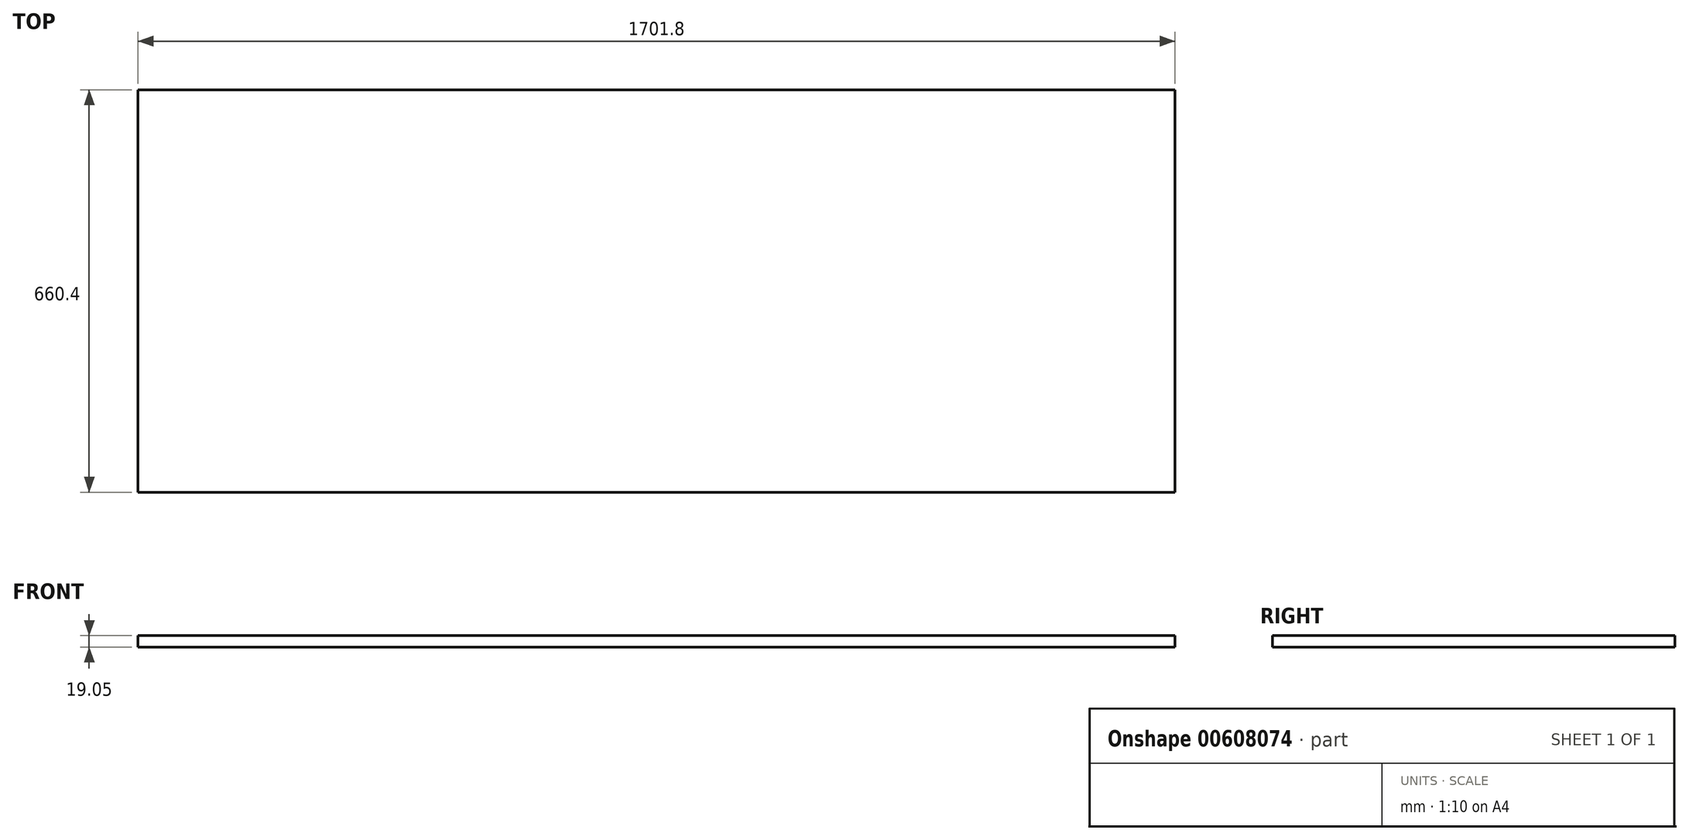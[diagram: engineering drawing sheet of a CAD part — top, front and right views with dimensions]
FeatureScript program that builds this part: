
annotation { "Feature Type Name" : "Feature", "Feature Type Description" : "" }
export const myFeature = defineFeature(function(context is Context, id is Id, definition is map)
    precondition{}
    {
        {
            var Q0;
            Q0=qCreatedBy(makeId("Top.planeOp"),FACE);
            var sketch = newSketch(context, id + "F0", { "sketchPlane" : qUnion([Q0])});
            skLineSegment(sketch, "E0.bottom", {"start": v(-850.9, 330.2) * mm, "end": v(850.9, 330.2) * mm});
            skLineSegment(sketch, "E0.top", {"start": v(-850.9, -330.2) * mm, "end": v(850.9, -330.2) * mm});
            skLineSegment(sketch, "E0.left", {"start": v(-850.9, 330.2) * mm, "end": v(-850.9, -330.2) * mm});
            skLineSegment(sketch, "E0.right", {"start": v(850.9, 330.2) * mm, "end": v(850.9, -330.2) * mm});
            skSolve(sketch);
        }
        {
            var Q0;
            Q0=makeQuery(id+"F0.imprint","IMPRINT",FACE,{"disambiguationData":[TD([[makeQuery(id+"F0.imprint","IMPRINT",EDGE,{"derivedFrom":sQuery(id+"F0.wireOp",EDGE,"E0.bottom")}),-1.0]])]});
            extrude(context, id + "F1", {"entities" : qUnion([Q0]), "depth" : 19.05 * mm, "offsetDistance" : 25.4 * mm});
        }
    });
